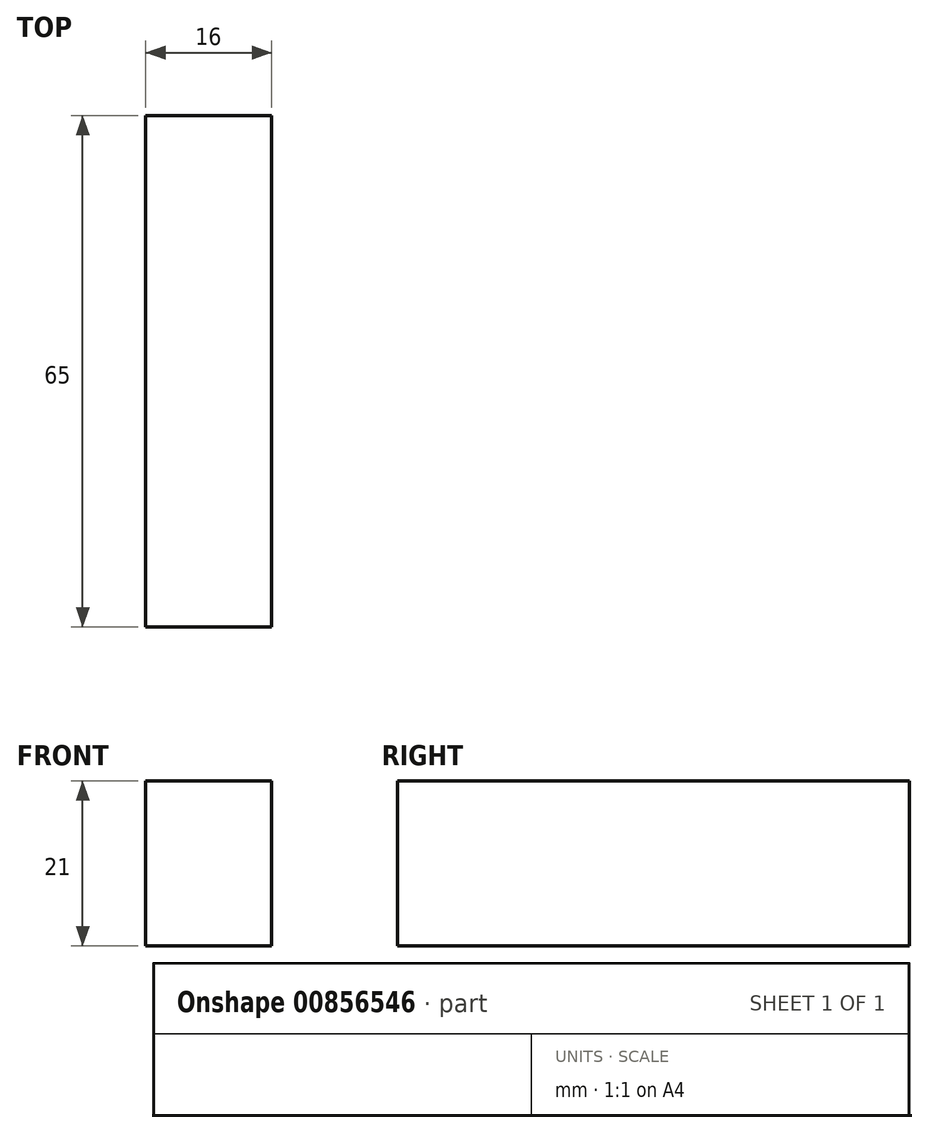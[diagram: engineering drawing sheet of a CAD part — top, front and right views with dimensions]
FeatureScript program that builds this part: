
annotation { "Feature Type Name" : "Feature", "Feature Type Description" : "" }
export const myFeature = defineFeature(function(context is Context, id is Id, definition is map)
    precondition{}
    {
        {
            var Q0;
            Q0=qCreatedBy(makeId("Top.planeOp"),FACE);
            var sketch = newSketch(context, id + "F0", { "sketchPlane" : qUnion([Q0])});
            skLineSegment(sketch, "E0.bottom", {"start": v(8, 32.5) * mm, "end": v(-8, 32.5) * mm});
            skLineSegment(sketch, "E0.top", {"start": v(8, -32.5) * mm, "end": v(-8, -32.5) * mm});
            skLineSegment(sketch, "E0.left", {"start": v(8, 32.5) * mm, "end": v(8, -32.5) * mm});
            skLineSegment(sketch, "E0.right", {"start": v(-8, 32.5) * mm, "end": v(-8, -32.5) * mm});
            skPoint(sketch, "E0.middle", {"position": v(0, 0) * mm});
            skSolve(sketch);
        }
        {
            var Q0;
            Q0 = qSketchRegion(id + "F0", true);
            extrude(context, id + "F1", {"entities" : qUnion([Q0]), "endBound" : BoundingType.SYMMETRIC, "depth" : 21 * mm, "offsetDistance" : 25 * mm});
        }
    });
